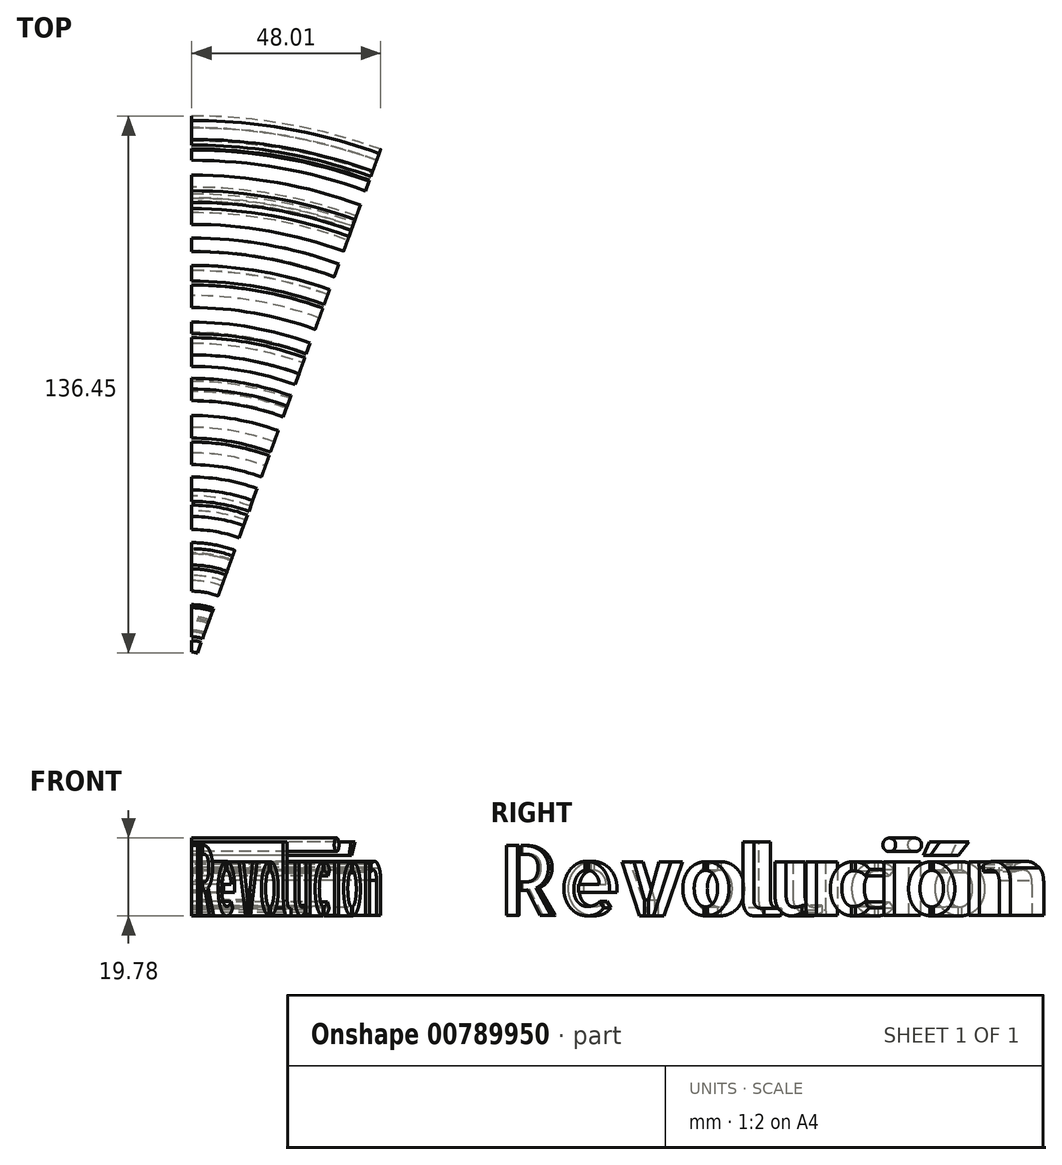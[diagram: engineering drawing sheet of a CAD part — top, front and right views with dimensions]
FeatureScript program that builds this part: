
annotation { "Feature Type Name" : "Feature", "Feature Type Description" : "" }
export const myFeature = defineFeature(function(context is Context, id is Id, definition is map)
    precondition{}
    {
        {
            var Q0;
            Q0=qCreatedBy(makeId("Right.planeOp"),FACE);
            var sketch = newSketch(context, id + "F0", { "sketchPlane" : qUnion([Q0])});
            skText(sketch, "E0", { "text": "Revolución", "fontName": "AllertaStencil-Regular.ttf"});
            skLineSegment(sketch, "E1", {"start": v(0, 71.64) * mm, "end": v(0, -67.66) * mm, "construction": true});
            const initialGuessF0  = {"E0": [0.002, 0.004, 1, 0, 0.01776]};
            skSetInitialGuess(sketch, initialGuessF0);
            skSolve(sketch);
        }
        {
            var Q0;
            Q0 = qSketchRegion(id + "F0", true);
            var Q1;
            Q1=sQuery(id+"F0.wireOp",EDGE,"E1");
            revolve(context, id + "F1", {"surfaceOperationType" : NewSurfaceOperationType.NEW, "entities" : qUnion([Q0]), "axis" : qUnion([Q1]), "revolveType" : RevolveType.ONE_DIRECTION, "angle" : 20 * degree});
        }
    });
